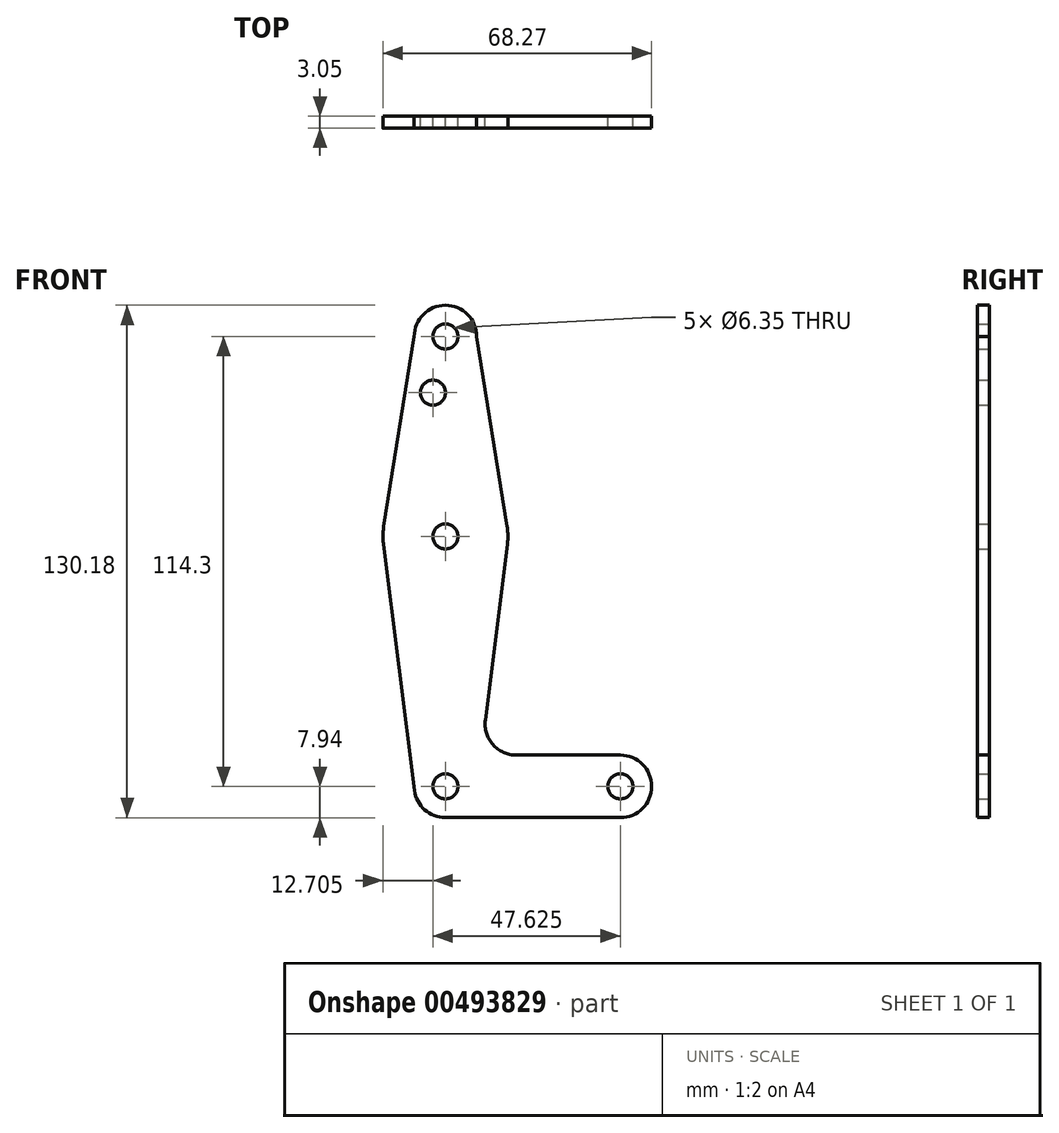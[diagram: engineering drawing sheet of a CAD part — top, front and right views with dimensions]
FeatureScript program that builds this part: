
annotation { "Feature Type Name" : "Feature", "Feature Type Description" : "" }
export const myFeature = defineFeature(function(context is Context, id is Id, definition is map)
    precondition{}
    {
        {
            var Q0;
            Q0=qCreatedBy(makeId("Front.planeOp"),FACE);
            var sketch = newSketch(context, id + "F0", { "sketchPlane" : qUnion([Q0])});
            skLineSegment(sketch, "E0", {"start": v(0, 0) * mm, "end": v(44.45, 0) * mm, "construction": true});
            skLineSegment(sketch, "E1", {"start": v(0, 0) * mm, "end": v(0, 114.3) * mm, "construction": true});
            skCircle(sketch, "E2", {"center": v(0, 114.3) * mm, "radius": 7.94 * mm});
            skCircle(sketch, "E3", {"center": v(44.45, 0) * mm, "radius": 7.94 * mm});
            skCircle(sketch, "E4", {"center": v(0, 63.5) * mm, "radius": 15.88 * mm});
            skCircle(sketch, "E5", {"center": v(0, 0) * mm, "radius": 7.94 * mm});
            skLineSegment(sketch, "E6", {"start": v(-7.94, 114.3) * mm, "end": v(-15.68, 66.01) * mm});
            skLineSegment(sketch, "E7", {"start": v(-15.75, 61.52) * mm, "end": v(-7.88, -1) * mm});
            skLineSegment(sketch, "E8", {"start": v(7.94, 114.3) * mm, "end": v(15.68, 66.01) * mm});
            skLineSegment(sketch, "E9", {"start": v(15.75, 61.52) * mm, "end": v(10.13, 16.88) * mm});
            skLineSegment(sketch, "E10", {"start": v(18.01, 7.94) * mm, "end": v(44.45, 7.94) * mm});
            skLineSegment(sketch, "E11", {"start": v(0, -7.94) * mm, "end": v(44.45, -7.94) * mm});
            skCircle(sketch, "E12", {"center": v(0, 63.5) * mm, "radius": 3.18 * mm});
            skCircle(sketch, "E13", {"center": v(0, 114.3) * mm, "radius": 3.18 * mm});
            skCircle(sketch, "E14", {"center": v(0, 0) * mm, "radius": 3.18 * mm});
            skCircle(sketch, "E15", {"center": v(44.45, 0) * mm, "radius": 3.18 * mm});
            skCircle(sketch, "E16", {"center": v(-3.18, 100.03) * mm, "radius": 3.18 * mm});
            skPoint(sketch, "E17.newPointA", {"position": v(7.88, -1) * mm});
            skArc(sketch, "E17.filletArc", {"start": v(10.13, 16.88) * mm, "mid": v(12.05, 10.63) * mm, "end": v(18.01, 7.94) * mm});
            skSolve(sketch);
        }
        {
            var Q0;
            Q0 = qSketchRegion(id + "F0", true);
            extrude(context, id + "F1", {"entities" : qUnion([Q0]), "depth" : 3.05 * mm});
        }
    });
